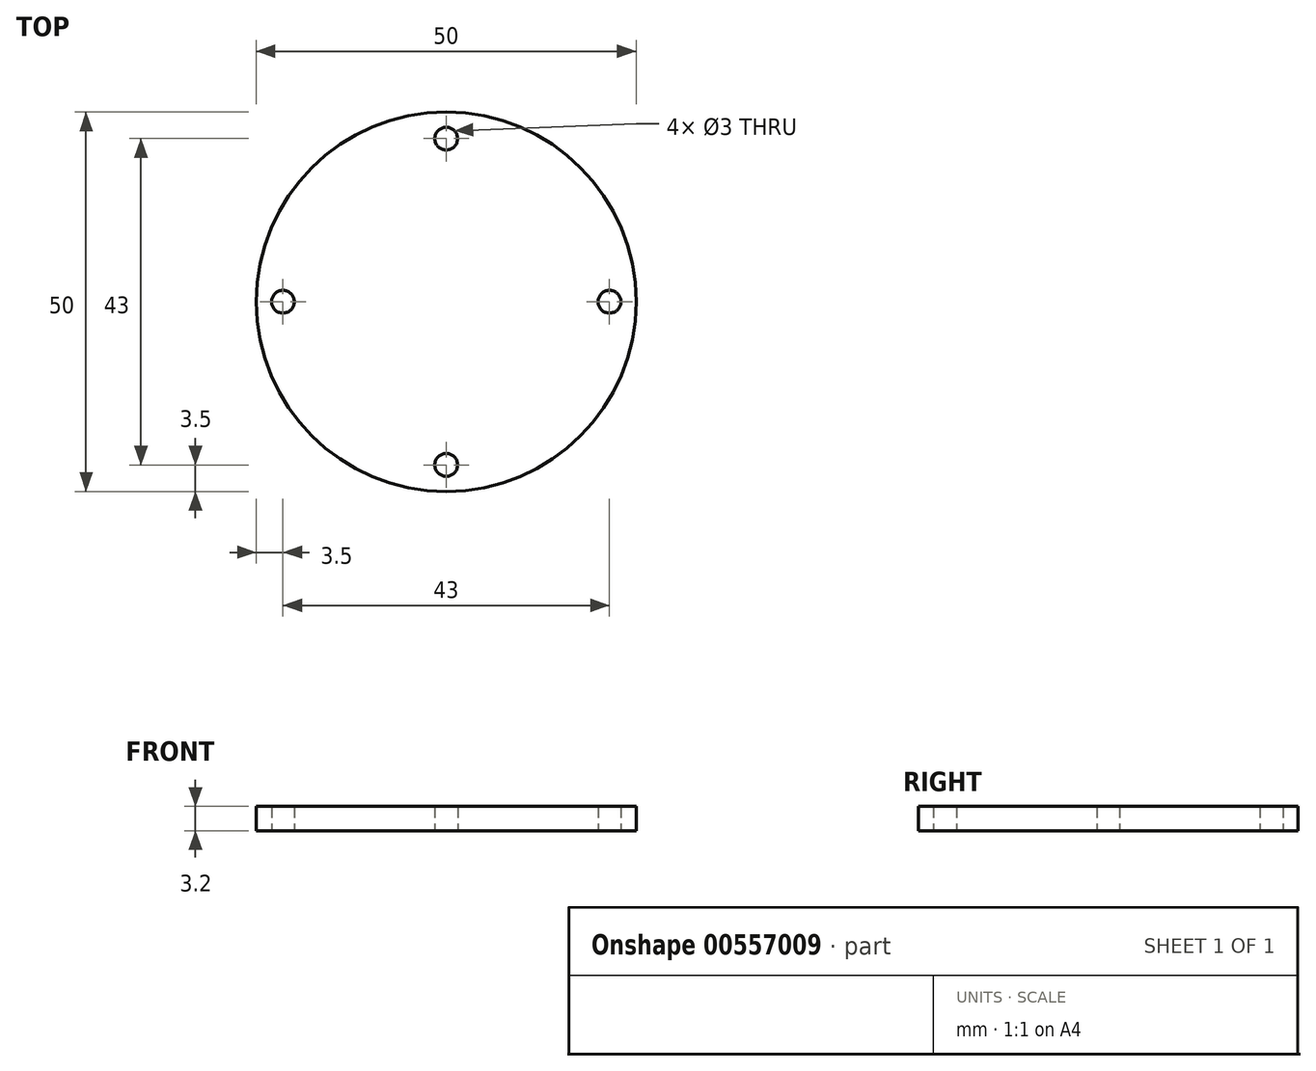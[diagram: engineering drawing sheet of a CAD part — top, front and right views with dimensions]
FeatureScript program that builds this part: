
annotation { "Feature Type Name" : "Feature", "Feature Type Description" : "" }
export const myFeature = defineFeature(function(context is Context, id is Id, definition is map)
    precondition{}
    {
        {
            var Q0;
            Q0=qCreatedBy(makeId("Top.planeOp"),FACE);
            var sketch = newSketch(context, id + "F0", { "sketchPlane" : qUnion([Q0])});
            skCircle(sketch, "E0", {"center": v(0, 0) * mm, "radius": 25 * mm});
            skCircle(sketch, "E1", {"center": v(0, 21.5) * mm, "radius": 1.5 * mm});
            skCircle(sketch, "E2", {"center": v(21.5, 0) * mm, "radius": 1.5 * mm});
            skCircle(sketch, "E3", {"center": v(0, -21.5) * mm, "radius": 1.5 * mm});
            skCircle(sketch, "E4", {"center": v(-21.5, 0) * mm, "radius": 1.5 * mm});
            skSolve(sketch);
        }
        {
            var Q0;
            Q0=qSketchRegion(id+"F0",true);
            extrude(context, id + "F1", {"entities" : qUnion([Q0]), "depth" : 3.2 * mm});
        }
    });
